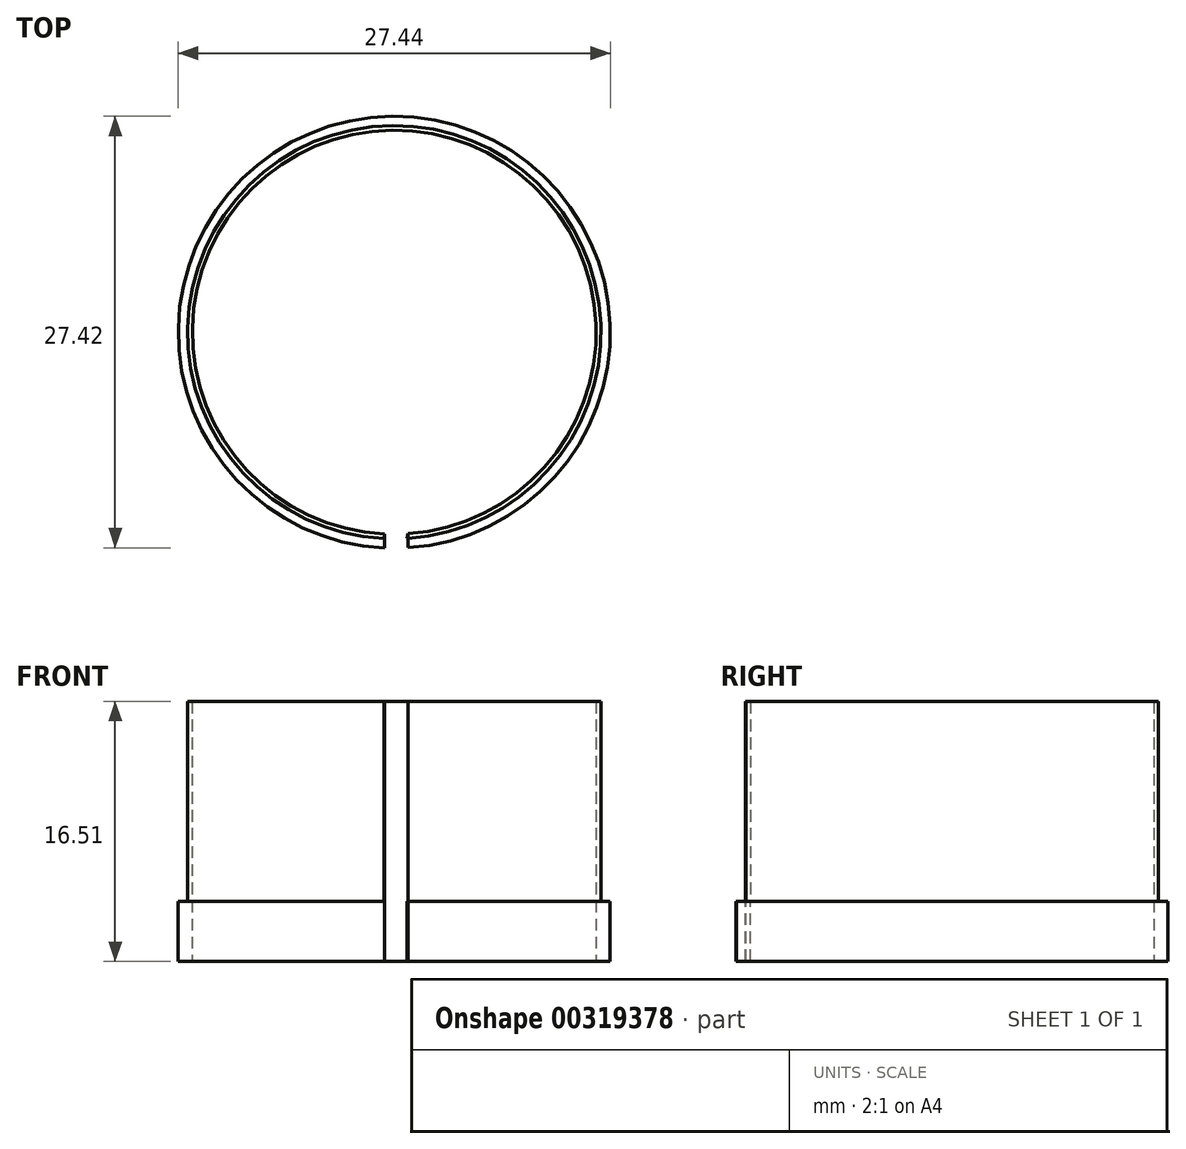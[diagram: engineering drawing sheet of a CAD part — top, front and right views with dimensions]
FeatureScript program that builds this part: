
annotation { "Feature Type Name" : "Feature", "Feature Type Description" : "" }
export const myFeature = defineFeature(function(context is Context, id is Id, definition is map)
    precondition{}
    {
        {
            var Q0;
            Q0=qCreatedBy(makeId("Top.planeOp"),FACE);
            var sketch = newSketch(context, id + "F0", { "sketchPlane" : qUnion([Q0])});
            skArc(sketch, "E0", {"start": v(0.87, -12.8) * mm, "mid": v(-0.12, 12.82) * mm, "end": v(-0.62, -12.81) * mm});
            skArc(sketch, "E1", {"start": v(0.83, -13.1) * mm, "mid": v(-0.08, 13.12) * mm, "end": v(-0.66, -13.1) * mm});
            skLineSegment(sketch, "E2.left", {"start": v(-0.62, -12.81) * mm, "end": v(-0.66, -13.1) * mm});
            skLineSegment(sketch, "E2.right", {"start": v(0.87, -12.8) * mm, "end": v(0.83, -13.1) * mm});
            skArc(sketch, "E3", {"start": v(0.87, -13.69) * mm, "mid": v(-0.12, 13.72) * mm, "end": v(-0.62, -13.7) * mm});
            skLineSegment(sketch, "E4", {"start": v(-0.62, -12.81) * mm, "end": v(-0.62, -13.7) * mm});
            skLineSegment(sketch, "E5", {"start": v(0.87, -12.8) * mm, "end": v(0.87, -13.69) * mm});
            skSolve(sketch);
        }
        {
            var Q0;
            {var subQ0=sQuery(id+"F0.wireOp",EDGE,"E0");Q0=makeQuery(id+"F0.imprint","IMPRINT",FACE,{"disambiguationData":[TD([[makeQuery(id+"F0.imprint","IMPRINT",EDGE,{"derivedFrom":subQ0}),-1.0]])]});}
            extrude(context, id + "F1", {"entities" : qUnion([Q0]), "depth" : 12.7 * mm});
        }
        {
            var Q0;
            Q0 = qSketchRegion(id + "F0", true);
            extrude(context, id + "F2", {"entities" : qUnion([Q0]), "operationType" : NewBodyOperationType.ADD, "oppositeDirection" : true, "depth" : 3.8 * mm});
        }
    });
